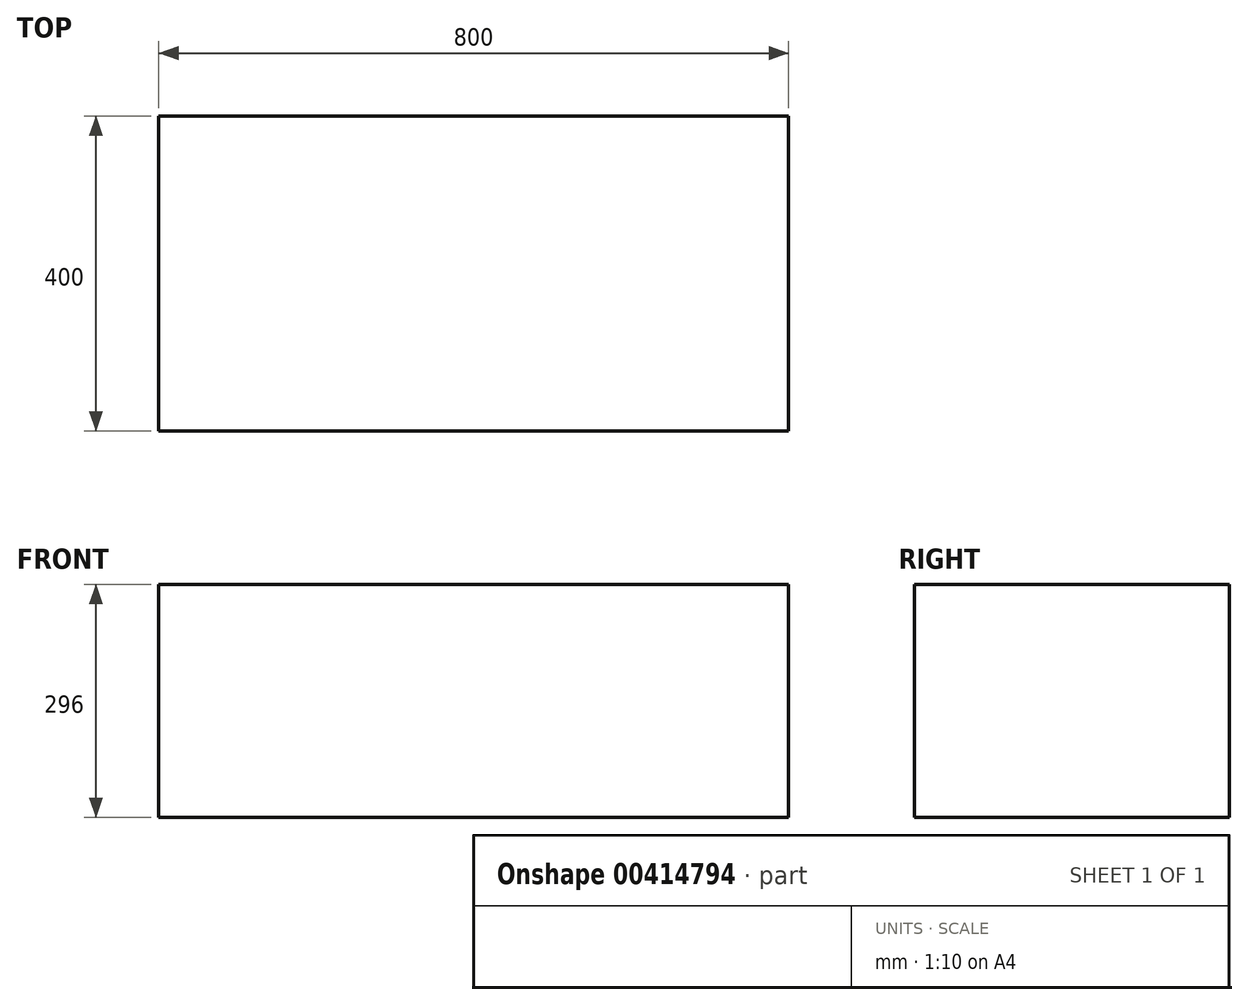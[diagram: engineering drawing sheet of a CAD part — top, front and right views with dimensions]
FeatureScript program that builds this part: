
annotation { "Feature Type Name" : "Feature", "Feature Type Description" : "" }
export const myFeature = defineFeature(function(context is Context, id is Id, definition is map)
    precondition{}
    {
        {
            var Q0;
            Q0=qCreatedBy(makeId("Front.planeOp"),FACE);
            var sketch = newSketch(context, id + "F0", { "sketchPlane" : qUnion([Q0])});
            skLineSegment(sketch, "E0", {"start": v(-377.53, -37.69) * mm, "end": v(422.47, -37.69) * mm});
            skLineSegment(sketch, "E1", {"start": v(-377.53, -37.69) * mm, "end": v(-377.53, -19.69) * mm});
            skLineSegment(sketch, "E2", {"start": v(-377.53, -19.69) * mm, "end": v(-377.53, 110.31) * mm});
            skLineSegment(sketch, "E3", {"start": v(-377.53, 110.31) * mm, "end": v(-377.53, 240.31) * mm});
            skLineSegment(sketch, "E4", {"start": v(-377.53, 240.31) * mm, "end": v(-377.53, 258.31) * mm});
            skLineSegment(sketch, "E5", {"start": v(-377.53, 258.31) * mm, "end": v(-359.53, 258.31) * mm});
            skLineSegment(sketch, "E6", {"start": v(422.47, 258.31) * mm, "end": v(422.47, -37.69) * mm});
            skLineSegment(sketch, "E7", {"start": v(-377.53, 240.31) * mm, "end": v(422.47, 240.31) * mm});
            skLineSegment(sketch, "E8", {"start": v(-359.53, 258.31) * mm, "end": v(-58.53, 258.31) * mm});
            skLineSegment(sketch, "E9", {"start": v(-359.53, 258.31) * mm, "end": v(-359.53, -37.69) * mm});
            skLineSegment(sketch, "E10", {"start": v(404.47, 258.31) * mm, "end": v(422.47, 258.31) * mm});
            skLineSegment(sketch, "E11", {"start": v(404.47, 258.31) * mm, "end": v(404.47, -37.69) * mm});
            skLineSegment(sketch, "E12", {"start": v(-377.53, -19.69) * mm, "end": v(422.47, -19.69) * mm});
            skLineSegment(sketch, "E13", {"start": v(-377.53, 110.31) * mm, "end": v(422.47, 110.31) * mm});
            skLineSegment(sketch, "E14", {"start": v(-40.53, 258.31) * mm, "end": v(404.47, 258.31) * mm});
            skLineSegment(sketch, "E15", {"start": v(-58.53, 258.31) * mm, "end": v(-40.53, 258.31) * mm});
            skLineSegment(sketch, "E16", {"start": v(-58.53, 258.31) * mm, "end": v(-58.53, -37.69) * mm});
            skLineSegment(sketch, "E17", {"start": v(-40.53, 258.31) * mm, "end": v(-40.53, -37.69) * mm});
            skSolve(sketch);
        }
        {
            var Q0;
            {var subQ0=sQuery(id+"F0.wireOp",EDGE,"E2");Q0=makeQuery(id+"F0.imprint","IMPRINT",FACE,{"disambiguationData":[TD([[makeQuery(id+"F0.imprint","IMPRINT",EDGE,{"derivedFrom":subQ0}),-1.0]])]});}
            var Q1;
            {var subQ0=sQuery(id+"F0.wireOp",EDGE,"E4");Q1=makeQuery(id+"F0.imprint","IMPRINT",FACE,{"disambiguationData":[TD([[makeQuery(id+"F0.imprint","IMPRINT",EDGE,{"derivedFrom":subQ0}),-1.0]])]});}
            var Q2;
            {var subQ0=sQuery(id+"F0.wireOp",EDGE,"E10");Q2=makeQuery(id+"F0.imprint","IMPRINT",FACE,{"disambiguationData":[TD([[makeQuery(id+"F0.imprint","IMPRINT",EDGE,{"derivedFrom":subQ0}),-1.0]])]});}
            var Q3;
            {var subQ0=sQuery(id+"F0.wireOp",EDGE,"E6");var subQ1=sQuery(id+"F0.wireOp",EDGE,"E0");var subQ2=makeQuery(id+"F0.imprint","INTERSECT",VERTEX,{"derivedFrom":[subQ1,subQ0]});Q3=makeQuery(id+"F0.imprint","IMPRINT",FACE,{"disambiguationData":[TD([[makeQuery(id+"F0.imprint","IMPRINT",EDGE,{"disambiguationData":[TD([[subQ2,1.0]])],"derivedFrom":subQ1}),1.0]])]});}
            var Q4;
            {var subQ0=sQuery(id+"F0.wireOp",EDGE,"E9");var subQ1=sQuery(id+"F0.wireOp",EDGE,"E7");var subQ2=makeQuery(id+"F0.imprint","INTERSECT",VERTEX,{"derivedFrom":[subQ1,subQ0]});Q4=makeQuery(id+"F0.imprint","IMPRINT",FACE,{"disambiguationData":[TD([[makeQuery(id+"F0.imprint","IMPRINT",EDGE,{"disambiguationData":[TD([[subQ2,-1.0]])],"derivedFrom":subQ1}),-1.0]])]});}
            var Q5;
            {var subQ0=sQuery(id+"F0.wireOp",EDGE,"E7");var subQ1=sQuery(id+"F0.wireOp",EDGE,"E6");var subQ2=makeQuery(id+"F0.imprint","INTERSECT",VERTEX,{"derivedFrom":[subQ1,subQ0]});Q5=makeQuery(id+"F0.imprint","IMPRINT",FACE,{"disambiguationData":[TD([[makeQuery(id+"F0.imprint","IMPRINT",EDGE,{"disambiguationData":[TD([[subQ2,-1.0]])],"derivedFrom":subQ1}),-1.0]])]});}
            var Q6;
            {var subQ5=sQuery(id+"F0.wireOp",EDGE,"E14");Q6=makeQuery(id+"F0.imprint","IMPRINT",FACE,{"disambiguationData":[TD([[makeQuery(id+"F0.imprint","IMPRINT",EDGE,{"derivedFrom":subQ5}),-1.0]])]});}
            var Q7;
            {var subQ0=sQuery(id+"F0.wireOp",EDGE,"E1");Q7=makeQuery(id+"F0.imprint","IMPRINT",FACE,{"disambiguationData":[TD([[makeQuery(id+"F0.imprint","IMPRINT",EDGE,{"derivedFrom":subQ0}),-1.0]])]});}
            var Q8;
            {var subQ0=sQuery(id+"F0.wireOp",EDGE,"E16");var subQ1=sQuery(id+"F0.wireOp",EDGE,"E7");var subQ2=makeQuery(id+"F0.imprint","INTERSECT",VERTEX,{"derivedFrom":[subQ1,subQ0]});Q8=makeQuery(id+"F0.imprint","IMPRINT",FACE,{"disambiguationData":[TD([[makeQuery(id+"F0.imprint","IMPRINT",EDGE,{"disambiguationData":[TD([[subQ2,-1.0]])],"derivedFrom":subQ1}),-1.0]])]});}
            var Q9;
            {var subQ0=sQuery(id+"F0.wireOp",EDGE,"E17");var subQ1=sQuery(id+"F0.wireOp",EDGE,"E7");var subQ2=makeQuery(id+"F0.imprint","INTERSECT",VERTEX,{"derivedFrom":[subQ1,subQ0]});Q9=makeQuery(id+"F0.imprint","IMPRINT",FACE,{"disambiguationData":[TD([[makeQuery(id+"F0.imprint","IMPRINT",EDGE,{"disambiguationData":[TD([[subQ2,-1.0]])],"derivedFrom":subQ1}),-1.0]])]});}
            var Q10;
            {var subQ0=sQuery(id+"F0.wireOp",EDGE,"E16");var subQ1=sQuery(id+"F0.wireOp",EDGE,"E0");var subQ2=makeQuery(id+"F0.imprint","INTERSECT",VERTEX,{"derivedFrom":[subQ1,subQ0]});Q10=makeQuery(id+"F0.imprint","IMPRINT",FACE,{"disambiguationData":[TD([[makeQuery(id+"F0.imprint","IMPRINT",EDGE,{"disambiguationData":[TD([[subQ2,-1.0]])],"derivedFrom":subQ1}),1.0]])]});}
            var Q11;
            {var subQ0=sQuery(id+"F0.wireOp",EDGE,"E13");var subQ1=sQuery(id+"F0.wireOp",EDGE,"E11");var subQ2=makeQuery(id+"F0.imprint","INTERSECT",VERTEX,{"derivedFrom":[subQ1,subQ0]});Q11=makeQuery(id+"F0.imprint","IMPRINT",FACE,{"disambiguationData":[TD([[makeQuery(id+"F0.imprint","IMPRINT",EDGE,{"disambiguationData":[TD([[subQ2,-1.0]])],"derivedFrom":subQ1}),-1.0]])]});}
            var Q12;
            {var subQ0=sQuery(id+"F0.wireOp",EDGE,"E13");var subQ1=sQuery(id+"F0.wireOp",EDGE,"E9");var subQ2=makeQuery(id+"F0.imprint","INTERSECT",VERTEX,{"derivedFrom":[subQ1,subQ0]});Q12=makeQuery(id+"F0.imprint","IMPRINT",FACE,{"disambiguationData":[TD([[makeQuery(id+"F0.imprint","IMPRINT",EDGE,{"disambiguationData":[TD([[subQ2,-1.0]])],"derivedFrom":subQ1}),1.0]])]});}
            var Q13;
            {var subQ0=sQuery(id+"F0.wireOp",EDGE,"E9");var subQ1=sQuery(id+"F0.wireOp",EDGE,"E0");var subQ2=makeQuery(id+"F0.imprint","INTERSECT",VERTEX,{"derivedFrom":[subQ1,subQ0]});Q13=makeQuery(id+"F0.imprint","IMPRINT",FACE,{"disambiguationData":[TD([[makeQuery(id+"F0.imprint","IMPRINT",EDGE,{"disambiguationData":[TD([[subQ2,-1.0]])],"derivedFrom":subQ1}),1.0]])]});}
            var Q14;
            {var subQ0=sQuery(id+"F0.wireOp",EDGE,"E11");var subQ1=sQuery(id+"F0.wireOp",EDGE,"E0");var subQ2=makeQuery(id+"F0.imprint","INTERSECT",VERTEX,{"derivedFrom":[subQ1,subQ0]});Q14=makeQuery(id+"F0.imprint","IMPRINT",FACE,{"disambiguationData":[TD([[makeQuery(id+"F0.imprint","IMPRINT",EDGE,{"disambiguationData":[TD([[subQ2,1.0]])],"derivedFrom":subQ1}),1.0]])]});}
            var Q15;
            {var subQ0=sQuery(id+"F0.wireOp",EDGE,"E3");Q15=makeQuery(id+"F0.imprint","IMPRINT",FACE,{"disambiguationData":[TD([[makeQuery(id+"F0.imprint","IMPRINT",EDGE,{"derivedFrom":subQ0}),-1.0]])]});}
            var Q16;
            {var subQ0=sQuery(id+"F0.wireOp",EDGE,"E16");var subQ1=sQuery(id+"F0.wireOp",EDGE,"E12");var subQ2=makeQuery(id+"F0.imprint","INTERSECT",VERTEX,{"derivedFrom":[subQ1,subQ0]});Q16=makeQuery(id+"F0.imprint","IMPRINT",FACE,{"disambiguationData":[TD([[makeQuery(id+"F0.imprint","IMPRINT",EDGE,{"disambiguationData":[TD([[subQ2,-1.0]])],"derivedFrom":subQ1}),1.0]])]});}
            var Q17;
            {var subQ0=sQuery(id+"F0.wireOp",EDGE,"E12");var subQ1=sQuery(id+"F0.wireOp",EDGE,"E6");var subQ2=makeQuery(id+"F0.imprint","INTERSECT",VERTEX,{"derivedFrom":[subQ1,subQ0]});Q17=makeQuery(id+"F0.imprint","IMPRINT",FACE,{"disambiguationData":[TD([[makeQuery(id+"F0.imprint","IMPRINT",EDGE,{"disambiguationData":[TD([[subQ2,1.0]])],"derivedFrom":subQ1}),-1.0]])]});}
            var Q18;
            {var subQ5=sQuery(id+"F0.wireOp",EDGE,"E8");Q18=makeQuery(id+"F0.imprint","IMPRINT",FACE,{"disambiguationData":[TD([[makeQuery(id+"F0.imprint","IMPRINT",EDGE,{"derivedFrom":subQ5}),-1.0]])]});}
            var Q19;
            {var subQ5=sQuery(id+"F0.wireOp",EDGE,"E15");Q19=makeQuery(id+"F0.imprint","IMPRINT",FACE,{"disambiguationData":[TD([[makeQuery(id+"F0.imprint","IMPRINT",EDGE,{"derivedFrom":subQ5}),-1.0]])]});}
            extrude(context, id + "F1", {"entities" : qUnion([Q0, Q1, Q2, Q3, Q4, Q5, Q6, Q7, Q8, Q9, Q10, Q11, Q12, Q13, Q14, Q15, Q16, Q17, Q18, Q19]), "oppositeDirection" : true, "depth" : 400 * mm});
        }
    });
